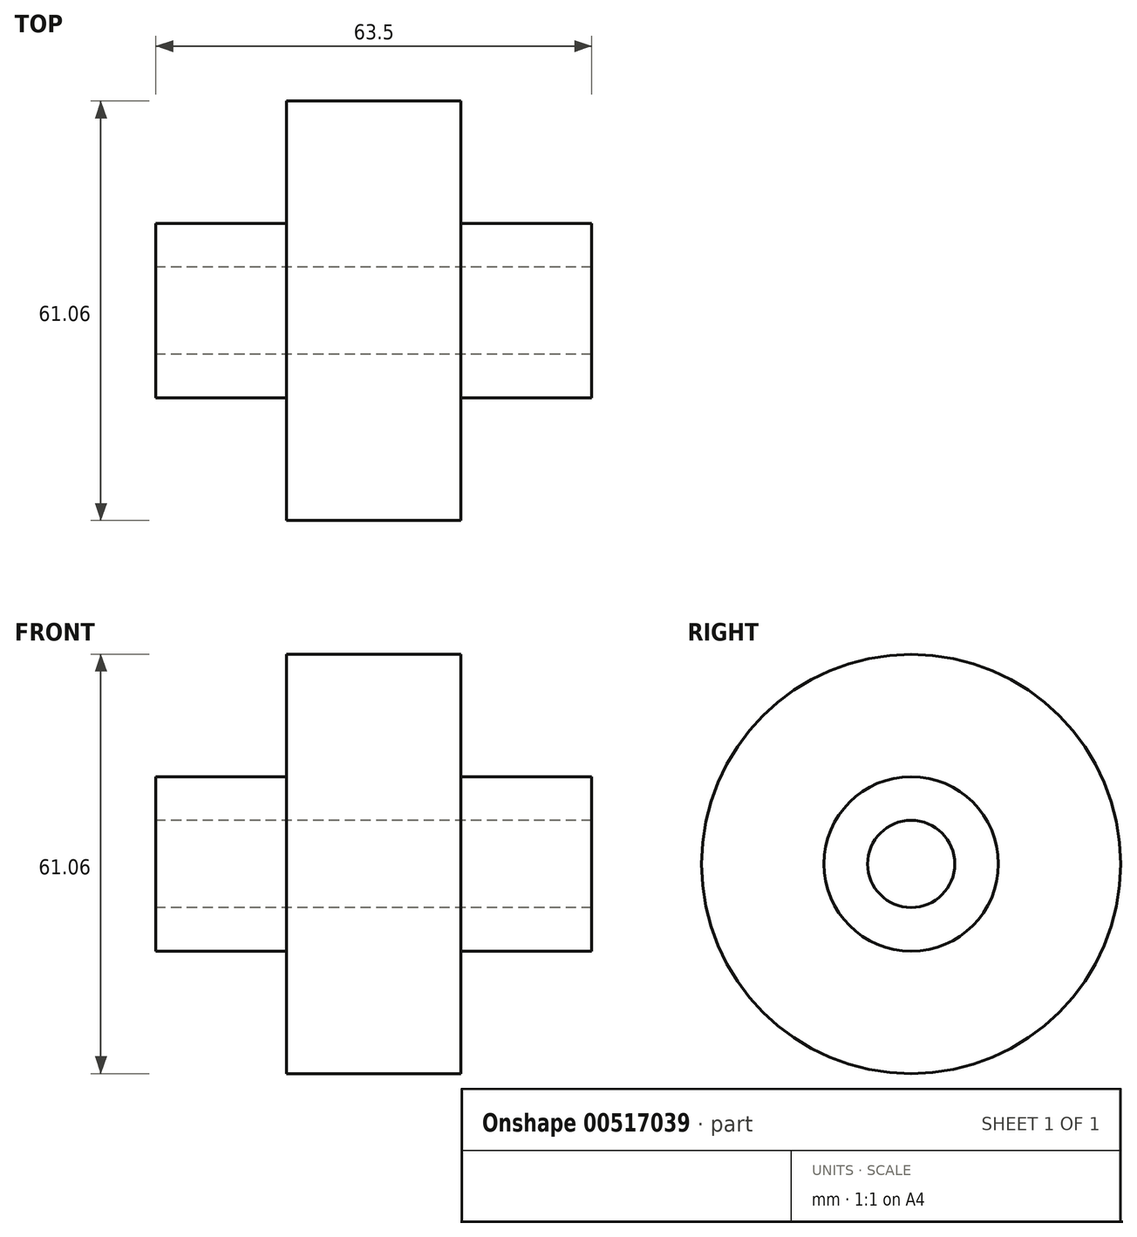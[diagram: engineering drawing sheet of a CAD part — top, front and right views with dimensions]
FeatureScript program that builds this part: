
annotation { "Feature Type Name" : "Feature", "Feature Type Description" : "" }
export const myFeature = defineFeature(function(context is Context, id is Id, definition is map)
    precondition{}
    {
        {
            var Q0;
            Q0=qCreatedBy(makeId("Front.planeOp"),FACE);
            var sketch = newSketch(context, id + "F0", { "sketchPlane" : qUnion([Q0])});
            skLineSegment(sketch, "E0", {"start": v(-54.59, 0) * mm, "end": v(54.59, 0) * mm, "construction": true});
            skPoint(sketch, "E1", {"position": v(0, 0) * mm});
            skLineSegment(sketch, "E2", {"start": v(-44.45, 6.35) * mm, "end": v(-44.45, 12.7) * mm});
            skLineSegment(sketch, "E3", {"start": v(-44.45, 12.7) * mm, "end": v(-25.4, 12.7) * mm});
            skLineSegment(sketch, "E4", {"start": v(-25.4, 12.7) * mm, "end": v(-25.4, 30.53) * mm});
            skLineSegment(sketch, "E5", {"start": v(-25.4, 30.53) * mm, "end": v(0, 30.53) * mm});
            skLineSegment(sketch, "E6", {"start": v(0, 30.53) * mm, "end": v(0, 12.7) * mm});
            skLineSegment(sketch, "E7", {"start": v(0, 12.7) * mm, "end": v(19.05, 12.7) * mm});
            skLineSegment(sketch, "E8", {"start": v(19.05, 12.7) * mm, "end": v(19.05, 6.35) * mm});
            skLineSegment(sketch, "E9", {"start": v(19.05, 6.35) * mm, "end": v(-44.45, 6.35) * mm});
            skSolve(sketch);
        }
        {
            var Q0;
            Q0=makeQuery(id+"F0.imprint","IMPRINT",FACE,{"disambiguationData":[TD([[makeQuery(id+"F0.imprint","IMPRINT",EDGE,{"derivedFrom":sQuery(id+"F0.wireOp",EDGE,"E2")}),-1.0]])]});
            var Q1;
            Q1=sQuery(id+"F0.wireOp",EDGE,"E0");
            revolve(context, id + "F1", {"entities" : qUnion([Q0]), "axis" : qUnion([Q1]), "revolveType" : RevolveType.FULL});
        }
    });
